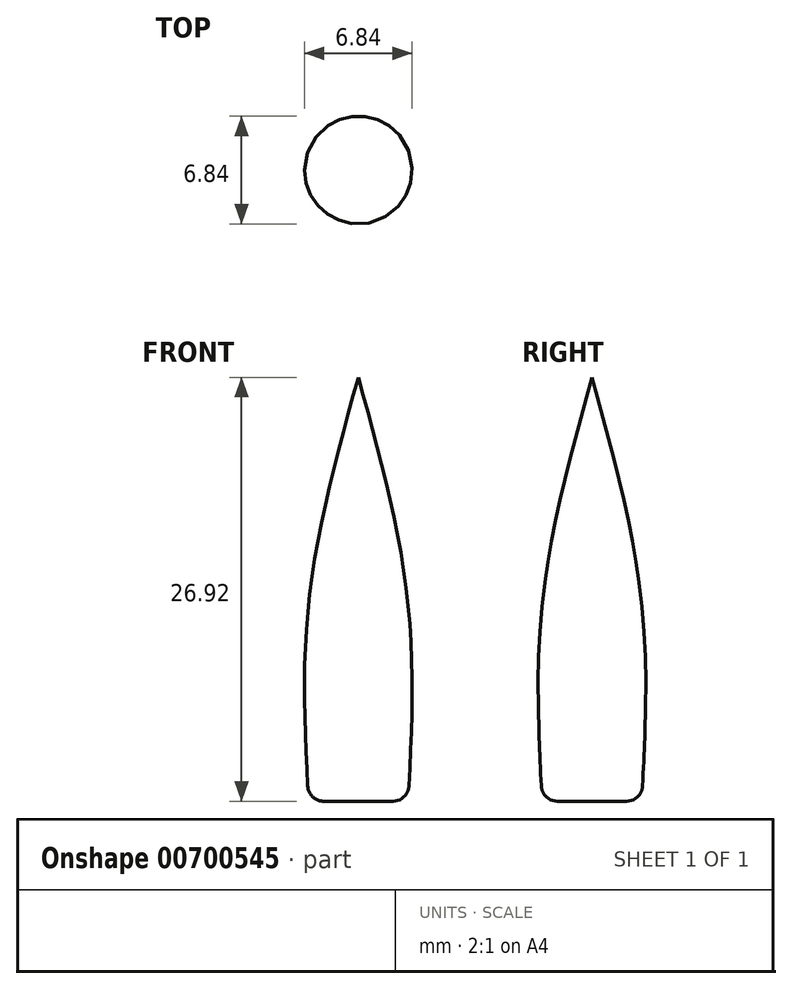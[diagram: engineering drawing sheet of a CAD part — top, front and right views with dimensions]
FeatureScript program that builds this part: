
annotation { "Feature Type Name" : "Feature", "Feature Type Description" : "" }
export const myFeature = defineFeature(function(context is Context, id is Id, definition is map)
    precondition{}
    {
        {
            var Q0;
            Q0=qCreatedBy(makeId("Front.planeOp"),FACE);
            var sketch = newSketch(context, id + "F0", { "sketchPlane" : qUnion([Q0])});
            skFitSpline(sketch, "E0", {"points": [v(-3.16, 0) * mm, v(-3.13, 12.78) * mm, v(0, 26.92) * mm], "startDerivative": vector(-1.48, 26.14) * mm, "endDerivative": vector(7.7, 27.68) * mm});
            skLineSegment(sketch, "E1", {"start": v(-3.16, 0) * mm, "end": v(0, 0) * mm});
            skLineSegment(sketch, "E2", {"start": v(0, 0) * mm, "end": v(0, 26.92) * mm});
            skSolve(sketch);
        }
        {
            var Q0;
            Q0=makeQuery(id+"F0.imprint","IMPRINT",FACE,{"disambiguationData":[TD([[makeQuery(id+"F0.imprint","IMPRINT",EDGE,{"derivedFrom":sQuery(id+"F0.wireOp",EDGE,"E0")}),-1.0]])]});
            var Q1;
            Q1=sQuery(id+"F0.wireOp",EDGE,"E2");
            revolve(context, id + "F1", {"entities" : qUnion([Q0]), "axis" : qUnion([Q1]), "revolveType" : RevolveType.FULL});
        }
        {
            var Q0;
            Q0=makeQuery(id+"F1.opRevolve","SWEPT_EDGE",EDGE,{"disambiguationData":[OSD([sQuery(id+"F0.wireOp",EDGE,"E0"),sQuery(id+"F0.wireOp",EDGE,"E1")])]});
            fillet(context, id + "F2", {"entities" : qUnion([Q0]), "radius" : 1.02 * mm, "tangentPropagation" : true, "allowEdgeOverflow" : false});
        }
    });
